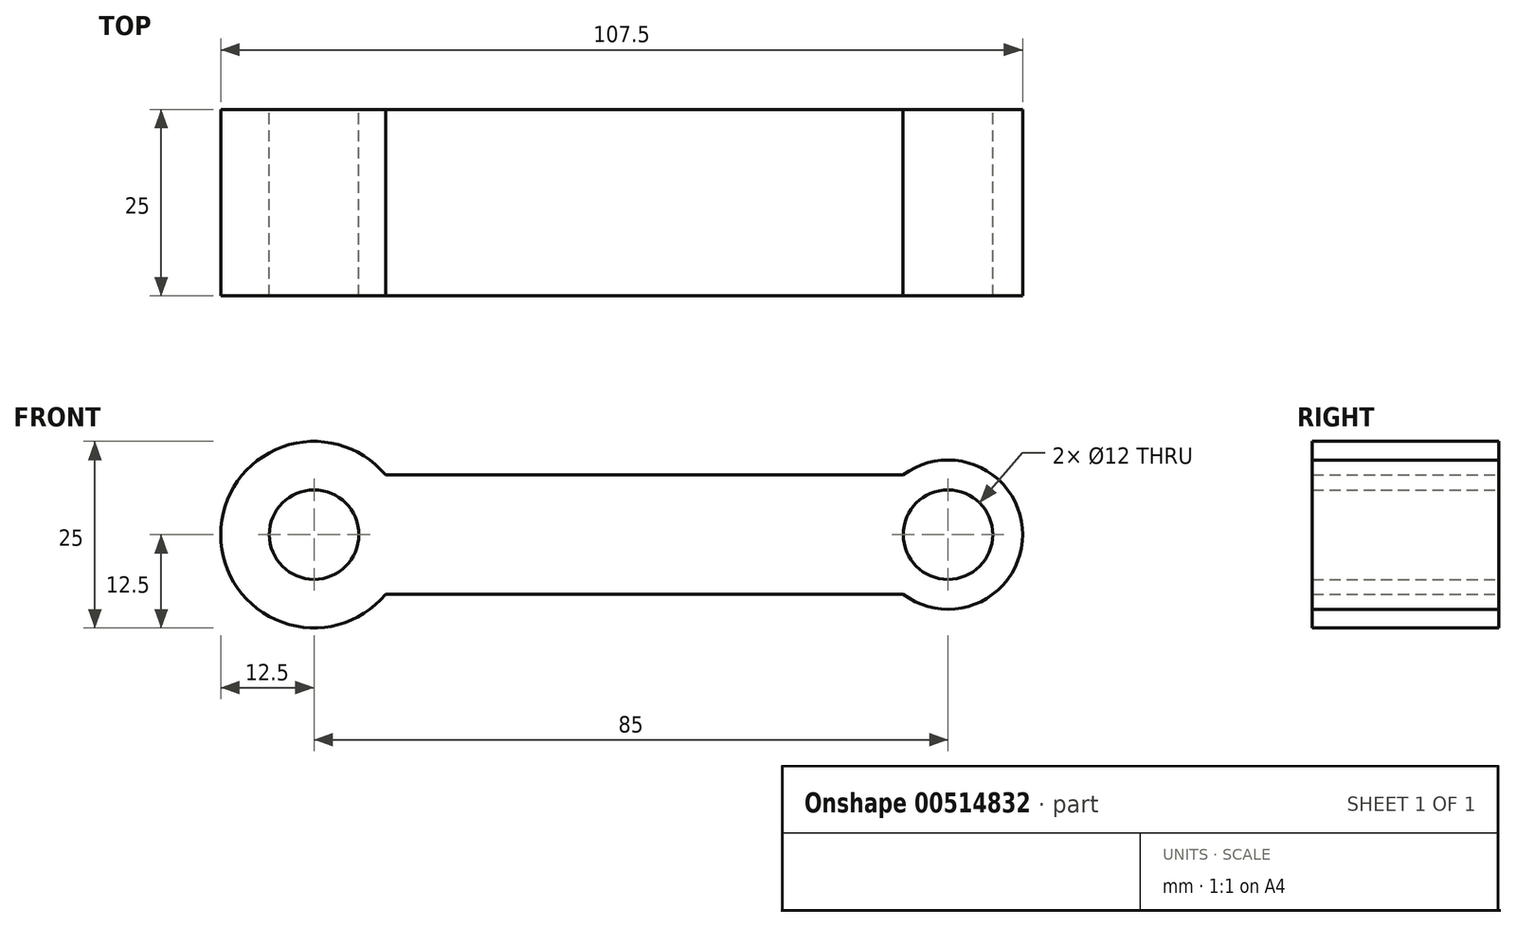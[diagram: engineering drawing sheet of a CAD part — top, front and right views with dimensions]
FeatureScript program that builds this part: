
annotation { "Feature Type Name" : "Feature", "Feature Type Description" : "" }
export const myFeature = defineFeature(function(context is Context, id is Id, definition is map)
    precondition{}
    {
        {
            var Q0;
            Q0=qCreatedBy(makeId("Front.planeOp"),FACE);
            var sketch = newSketch(context, id + "F0", { "sketchPlane" : qUnion([Q0])});
            skCircle(sketch, "E0", {"center": v(0, 0) * mm, "radius": 12.5 * mm});
            skCircle(sketch, "E1", {"center": v(85, 0) * mm, "radius": 10 * mm});
            skLineSegment(sketch, "E2", {"start": v(9.6, 8.02) * mm, "end": v(78.98, 7.98) * mm});
            skLineSegment(sketch, "E3", {"start": v(0, 0) * mm, "end": v(85, 0) * mm, "construction": true});
            skLineSegment(sketch, "E4.MirrorCS", {"start": v(9.6, -8.02) * mm, "end": v(78.98, -7.98) * mm});
            skCircle(sketch, "E5", {"center": v(0, 0) * mm, "radius": 6 * mm});
            skCircle(sketch, "E6", {"center": v(85, 0) * mm, "radius": 6 * mm});
            skPoint(sketch, "E7.startSnap0", {"position": v(44.28, 8) * mm});
            skPoint(sketch, "E7.endSnap0", {"position": v(44.28, 8) * mm});
            skSolve(sketch);
        }
        {
            var Q0;
            Q0 = qSketchRegion(id + "F0", true);
            extrude(context, id + "F1", {"entities" : qUnion([Q0]), "depth" : 25 * mm, "offsetDistance" : 25 * mm});
        }
    });
